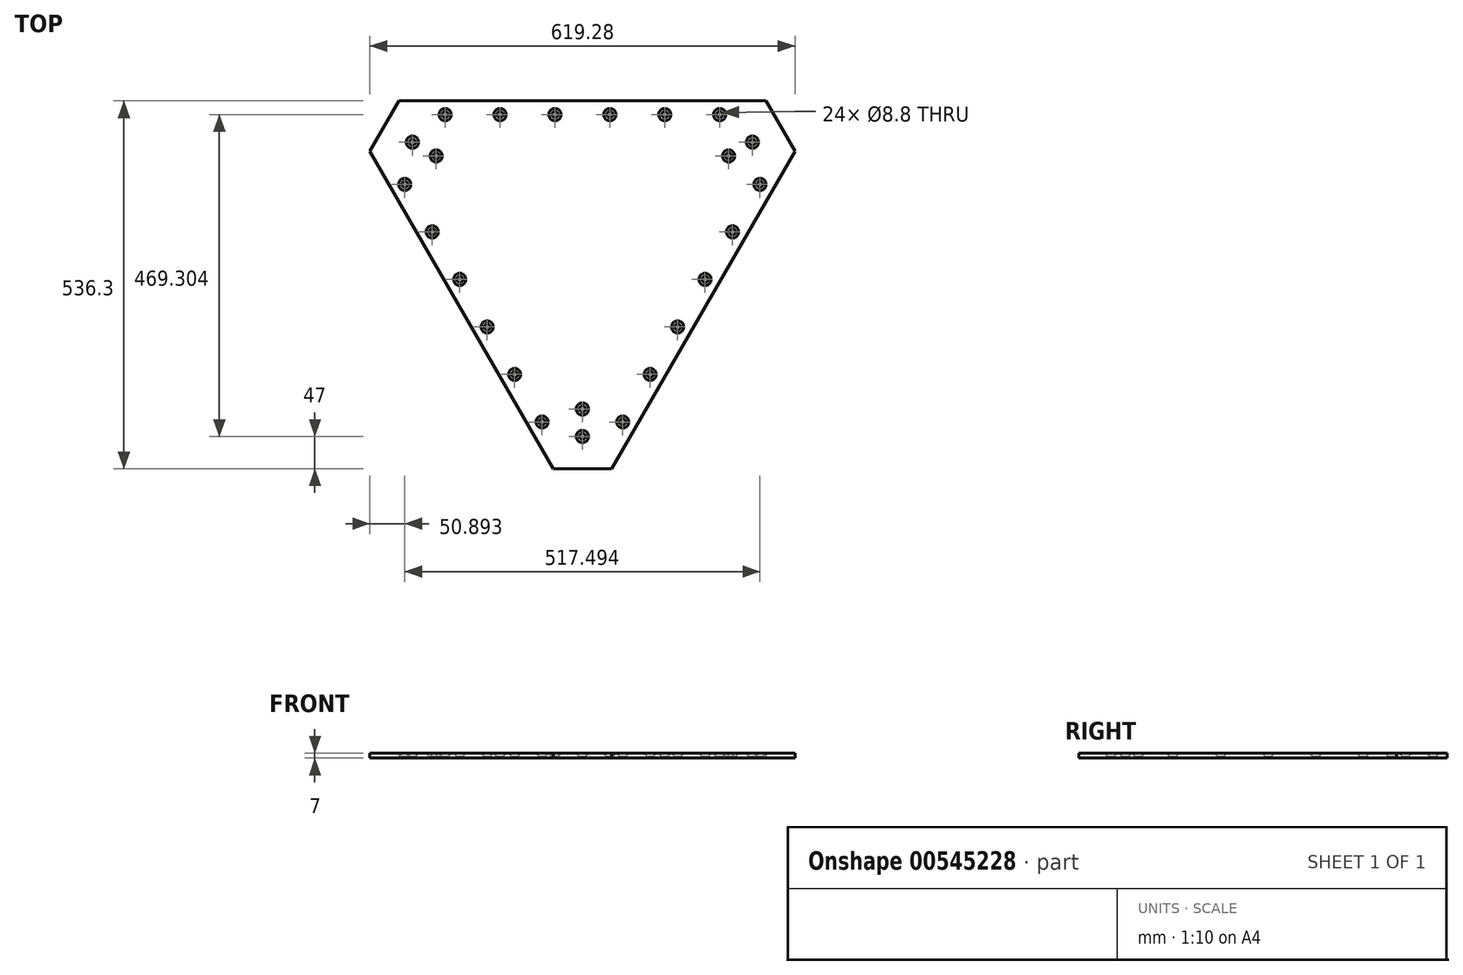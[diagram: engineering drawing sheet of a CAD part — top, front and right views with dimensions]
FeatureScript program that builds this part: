
annotation { "Feature Type Name" : "Feature", "Feature Type Description" : "" }
export const myFeature = defineFeature(function(context is Context, id is Id, definition is map)
    precondition{}
    {
        {
            var Q0;
            Q0=qCreatedBy(makeId("Top.planeOp"),FACE);
            var sketch = newSketch(context, id + "F0", { "sketchPlane" : qUnion([Q0])});
            skLineSegment(sketch, "E0", {"start": v(-42.5, 0) * mm, "end": v(42.5, 0) * mm});
            skPoint(sketch, "E1.orphan", {"position": v(-85, 73.61) * mm});
            skPoint(sketch, "E2.orphan", {"position": v(85, 73.61) * mm});
            skLineSegment(sketch, "E3", {"start": v(-42.5, 0) * mm, "end": v(-309.64, 462.7) * mm});
            skLineSegment(sketch, "E4.MirrorCS", {"start": v(42.5, 0) * mm, "end": v(309.64, 462.7) * mm});
            skLineSegment(sketch, "E5", {"start": v(-309.64, 462.7) * mm, "end": v(-267.14, 536.3) * mm});
            skLineSegment(sketch, "E6", {"start": v(-267.14, 536.3) * mm, "end": v(267.14, 536.3) * mm});
            skLineSegment(sketch, "E7", {"start": v(267.14, 536.3) * mm, "end": v(309.64, 462.7) * mm});
            skPoint(sketch, "E8.orphan", {"position": v(-53.76, 19.5) * mm});
            skPoint(sketch, "E9.orphan", {"position": v(53.76, 19.5) * mm});
            skLineSegment(sketch, "E10", {"start": v(-108.97, 47) * mm, "end": v(171.23, 47) * mm, "construction": true});
            skLineSegment(sketch, "E11", {"start": v(69.64, 47) * mm, "end": v(309.64, 462.7) * mm});
            skLineSegment(sketch, "E12.MirrorCS", {"start": v(-69.64, 47) * mm, "end": v(-309.64, 462.7) * mm});
            skSolve(sketch);
        }
        {
            var Q0;
            Q0=makeQuery(id+"F0.imprint","IMPRINT",FACE,{"disambiguationData":[TD([[makeQuery(id+"F0.imprint","IMPRINT",EDGE,{"derivedFrom":sQuery(id+"F0.wireOp",EDGE,"E0")}),1.0]])]});
            extrude(context, id + "F1", {"entities" : qUnion([Q0]), "depth" : 7 * mm, "offsetDistance" : 25 * mm});
        }
        {
            var Q0;
            Q0=makeQuery(id+"F1.opExtrude","CAP_FACE",FACE,{"disambiguationData":[OSD([sQuery(id+"F0.wireOp",EDGE,"E0"),sQuery(id+"F0.wireOp",EDGE,"CaBQzmE1-p9BO-8GB0-kwD7-5pXdWfkqItnF"),sQuery(id+"F0.wireOp",EDGE,"41d334b9-8b63-40d4-95e3-e86603cb62630.MirrorCS"),sQuery(id+"F0.wireOp",EDGE,"ZMD3KIoU-Osl8-XbeK-J56L-HnU5Kfb2em0M")])],"isStart":false});
            var sketch = newSketch(context, id + "F2", { "sketchPlane" : qUnion([Q0])});
            skPoint(sketch, "E13", {"position": v(0, 47) * mm});
            skLineSegment(sketch, "E14", {"start": v(-318, 516.6) * mm, "end": v(-133.31, 409.97) * mm, "construction": true});
            skPoint(sketch, "E15", {"position": v(-247.68, 476) * mm});
            skLineSegment(sketch, "E16", {"start": v(346.72, 533.18) * mm, "end": v(173.42, 433.12) * mm, "construction": true});
            skPoint(sketch, "E17", {"position": v(247.68, 476) * mm});
            skSolve(sketch);
        }
        {
            var Q0;
            Q0=sQuery(id+"F2.wireOp",VERTEX,"E15");
            var Q1;
            Q1=sQuery(id+"F2.wireOp",VERTEX,"E17");
            var Q2;
            Q2=sQuery(id+"F2.wireOp",VERTEX,"E13");
            var Q3;
            Q3=makeQuery(id+"F1.opExtrude","SWEPT_BODY",BODY,{"disambiguationData":[OSD([sQuery(id+"F0.wireOp",EDGE,"E0"),sQuery(id+"F0.wireOp",EDGE,"CaBQzmE1-p9BO-8GB0-kwD7-5pXdWfkqItnF"),sQuery(id+"F0.wireOp",EDGE,"41d334b9-8b63-40d4-95e3-e86603cb62630.MirrorCS"),sQuery(id+"F0.wireOp",EDGE,"ZMD3KIoU-Osl8-XbeK-J56L-HnU5Kfb2em0M")])]});
            hole(context, id + "F3", {"style" : HoleStyle.C_SINK, "endStyle" : HoleEndStyle.THROUGH, "standardTappedOrClearance" : lookupTablePath({ "standard" : "ISO", "fit" : "Normal", "size" : "M8", "type" : "Clearance" }), "standardBlindInLast" : lookupTablePath({ "fit" : "Standard", "standard" : "ISO", "size" : "M8", "type" : "Clearance" }), "holeDiameter" : 8.8 * mm, "cSinkDiameter" : 17.92 * mm, "cSinkAngle" : 90 * degree, "isTappedThrough" : true, "tappedDepth" : 12 * mm, "tapClearance" : 3, "locations" : qUnion([Q0, Q1, Q2]), "scope" : qUnion([Q3])});
        }
        {
            var Q0;
            Q0=makeQuery(id+"F1.opExtrude","CAP_FACE",FACE,{"disambiguationData":[OSD([sQuery(id+"F0.wireOp",EDGE,"E0"),sQuery(id+"F0.wireOp",EDGE,"E3"),sQuery(id+"F0.wireOp",EDGE,"E4.MirrorCS"),sQuery(id+"F0.wireOp",EDGE,"E5"),sQuery(id+"F0.wireOp",EDGE,"E6"),sQuery(id+"F0.wireOp",EDGE,"E7")])],"isStart":false});
            var sketch = newSketch(context, id + "F4", { "sketchPlane" : qUnion([Q0])});
            skLineSegment(sketch, "E18", {"start": v(298.09, 482.7) * mm, "end": v(19.4, 0) * mm, "construction": true});
            skPoint(sketch, "E19", {"position": v(398.52, 656.64) * mm});
            skPoint(sketch, "E20", {"position": v(438.52, 725.93) * mm});
            skLineSegment(sketch, "E21", {"start": v(0, 333) * mm, "end": v(400.6, 101.72) * mm, "construction": true});
            skPoint(sketch, "E22", {"position": v(58.75, 68.14) * mm});
            skPoint(sketch, "E23", {"position": v(98.75, 137.42) * mm});
            skPoint(sketch, "E24", {"position": v(138.75, 206.7) * mm});
            skPoint(sketch, "E25.MirrorP", {"position": v(258.75, 414.55) * mm});
            skPoint(sketch, "E26.MirrorP", {"position": v(218.75, 345.27) * mm});
            skPoint(sketch, "E27.MirrorP", {"position": v(178.75, 275.99) * mm});
            skLineSegment(sketch, "E28.MirrorCS", {"start": v(-298.09, 482.7) * mm, "end": v(-19.4, 0) * mm, "construction": true});
            skLineSegment(sketch, "E29.MirrorCS", {"start": v(0, 333) * mm, "end": v(-400.6, 101.72) * mm, "construction": true});
            skPoint(sketch, "E30.MirrorP", {"position": v(-58.75, 68.14) * mm});
            skPoint(sketch, "E31.MirrorP", {"position": v(-98.75, 137.42) * mm});
            skPoint(sketch, "E32.MirrorP", {"position": v(-138.75, 206.7) * mm});
            skPoint(sketch, "E33.MirrorP", {"position": v(-178.75, 275.99) * mm});
            skPoint(sketch, "E34.MirrorP", {"position": v(-218.75, 345.27) * mm});
            skPoint(sketch, "E35.MirrorP", {"position": v(-258.75, 414.55) * mm});
            skLineSegment(sketch, "E36", {"start": v(0, 333) * mm, "end": v(0, 645.15) * mm, "construction": true});
            skPoint(sketch, "E36.endSnap0", {"position": v(0, 536.3) * mm});
            skLineSegment(sketch, "E37", {"start": v(-278.68, 516.3) * mm, "end": v(278.68, 516.3) * mm, "construction": true});
            skPoint(sketch, "E38", {"position": v(200, 516.3) * mm});
            skPoint(sketch, "E39.1.0.0", {"position": v(120, 516.3) * mm});
            skPoint(sketch, "E39.2.0.0", {"position": v(40, 516.3) * mm});
            skLineSegment(sketch, "E39.direction1", {"start": v(200, 516.3) * mm, "end": v(120, 516.3) * mm, "construction": true});
            skPoint(sketch, "E40.MirrorP", {"position": v(-40, 516.3) * mm});
            skPoint(sketch, "E41.MirrorP", {"position": v(-120, 516.3) * mm});
            skPoint(sketch, "E42.MirrorP", {"position": v(-200, 516.3) * mm});
            skLineSegment(sketch, "E43", {"start": v(-315.56, 515.19) * mm, "end": v(0, 333) * mm, "construction": true});
            skPoint(sketch, "E44", {"position": v(-213.04, 456) * mm});
            skLineSegment(sketch, "E45", {"start": v(0, 333) * mm, "end": v(0, -50.5) * mm, "construction": true});
            skLineSegment(sketch, "E46.MirrorCS", {"start": v(315.56, 515.19) * mm, "end": v(0, 333) * mm, "construction": true});
            skPoint(sketch, "E47.MirrorP", {"position": v(213.04, 456) * mm});
            skPoint(sketch, "E48", {"position": v(0, 87) * mm});
            skSolve(sketch);
        }
        {
            var Q0;
            Q0=sQuery(id+"F4.wireOp",VERTEX,"E42.MirrorP");
            var Q1;
            Q1=sQuery(id+"F4.wireOp",VERTEX,"E41.MirrorP");
            var Q2;
            Q2=sQuery(id+"F4.wireOp",VERTEX,"E40.MirrorP");
            var Q3;
            Q3=sQuery(id+"F4.wireOp",VERTEX,"E39.2.0.0");
            var Q4;
            Q4=sQuery(id+"F4.wireOp",VERTEX,"E39.1.0.0");
            var Q5;
            Q5=sQuery(id+"F4.wireOp",VERTEX,"E38");
            var Q6;
            Q6=sQuery(id+"F4.wireOp",VERTEX,"E35.MirrorP");
            var Q7;
            Q7=sQuery(id+"F4.wireOp",VERTEX,"E34.MirrorP");
            var Q8;
            Q8=sQuery(id+"F4.wireOp",VERTEX,"E33.MirrorP");
            var Q9;
            Q9=sQuery(id+"F4.wireOp",VERTEX,"E32.MirrorP");
            var Q10;
            Q10=sQuery(id+"F4.wireOp",VERTEX,"E31.MirrorP");
            var Q11;
            Q11=sQuery(id+"F4.wireOp",VERTEX,"E30.MirrorP");
            var Q12;
            Q12=sQuery(id+"F4.wireOp",VERTEX,"E22");
            var Q13;
            Q13=sQuery(id+"F4.wireOp",VERTEX,"E23");
            var Q14;
            Q14=sQuery(id+"F4.wireOp",VERTEX,"E24");
            var Q15;
            Q15=sQuery(id+"F4.wireOp",VERTEX,"E27.MirrorP");
            var Q16;
            Q16=sQuery(id+"F4.wireOp",VERTEX,"E26.MirrorP");
            var Q17;
            Q17=sQuery(id+"F4.wireOp",VERTEX,"E25.MirrorP");
            var Q18;
            Q18=sQuery(id+"F4.wireOp",VERTEX,"E48");
            var Q19;
            Q19=sQuery(id+"F4.wireOp",VERTEX,"E44");
            var Q20;
            Q20=sQuery(id+"F4.wireOp",VERTEX,"E47.MirrorP");
            var Q21;
            Q21=makeQuery(id+"F1.opExtrude","SWEPT_BODY",BODY,{"disambiguationData":[OSD([sQuery(id+"F0.wireOp",EDGE,"E0"),sQuery(id+"F0.wireOp",EDGE,"E3"),sQuery(id+"F0.wireOp",EDGE,"E4.MirrorCS"),sQuery(id+"F0.wireOp",EDGE,"E5"),sQuery(id+"F0.wireOp",EDGE,"E6"),sQuery(id+"F0.wireOp",EDGE,"E7"),sQuery(id+"F0.wireOp",EDGE,"E11"),sQuery(id+"F0.wireOp",EDGE,"E12.MirrorCS")])]});
            hole(context, id + "F5", {"style" : HoleStyle.C_SINK, "endStyle" : HoleEndStyle.THROUGH, "standardTappedOrClearance" : lookupTablePath({ "standard" : "ISO", "fit" : "Normal", "size" : "M8", "type" : "Clearance" }), "standardBlindInLast" : lookupTablePath({ "fit" : "Standard", "standard" : "ISO", "size" : "M8", "type" : "Clearance" }), "holeDiameter" : 8.8 * mm, "cSinkDiameter" : 17.92 * mm, "cSinkAngle" : 90 * degree, "isTappedThrough" : true, "tappedDepth" : 12 * mm, "tapClearance" : 3, "locations" : qUnion([Q0, Q1, Q2, Q3, Q4, Q5, Q6, Q7, Q8, Q9, Q10, Q11, Q12, Q13, Q14, Q15, Q16, Q17, Q18, Q19, Q20]), "scope" : qUnion([Q21])});
        }
    });
